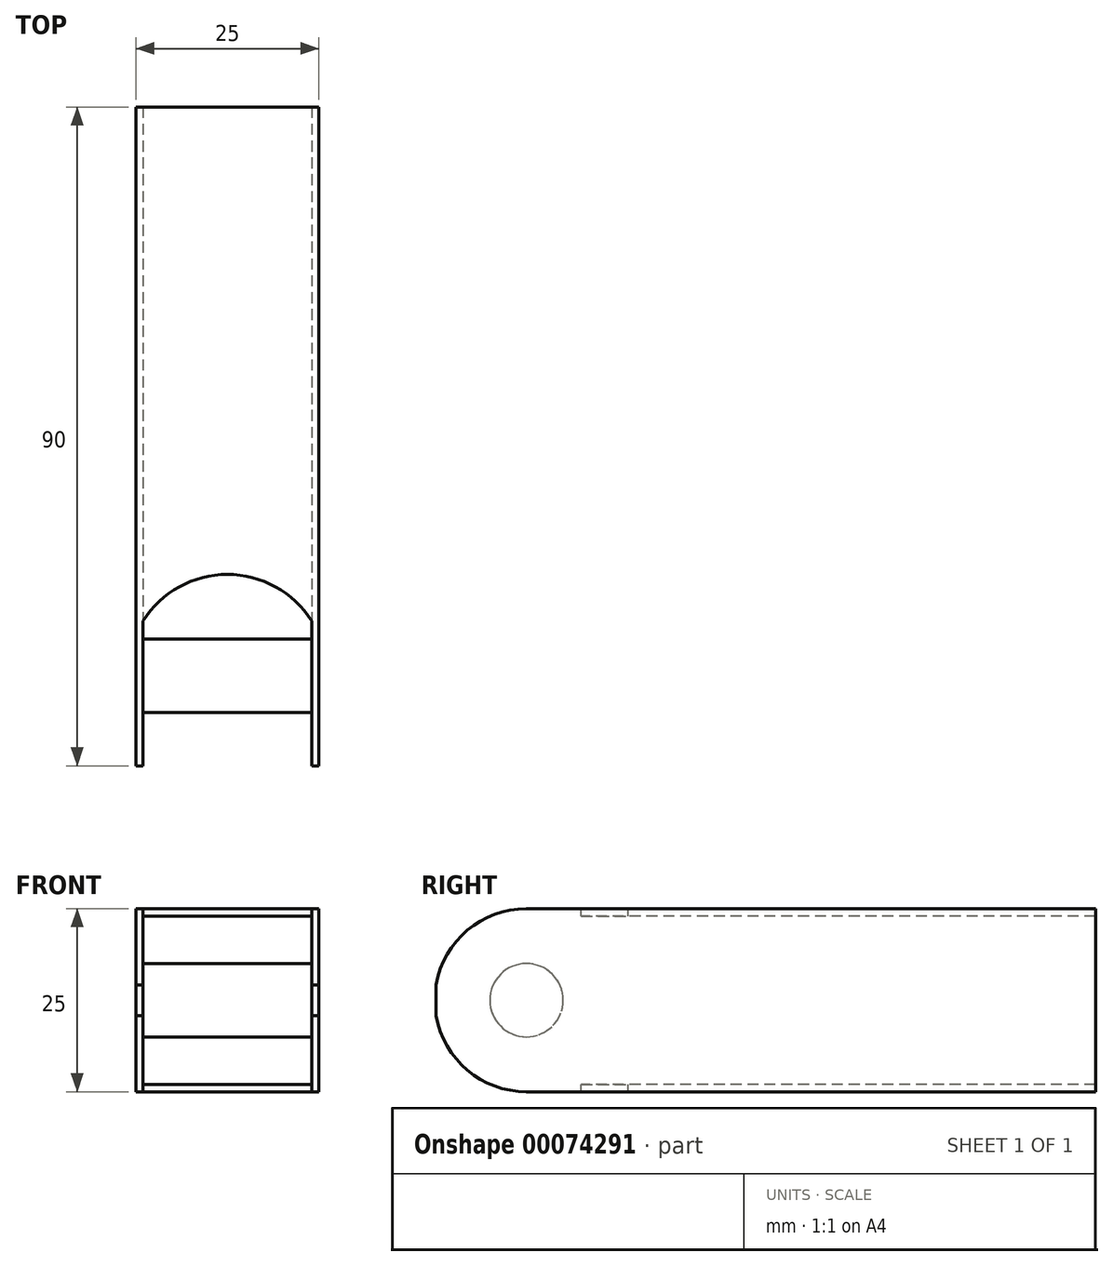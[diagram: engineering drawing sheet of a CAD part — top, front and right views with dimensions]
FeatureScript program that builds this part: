
annotation { "Feature Type Name" : "Feature", "Feature Type Description" : "" }
export const myFeature = defineFeature(function(context is Context, id is Id, definition is map)
    precondition{}
    {
        {
            var Q0;
            Q0=qCreatedBy(makeId("Front.planeOp"),FACE);
            var sketch = newSketch(context, id + "F0", { "sketchPlane" : qUnion([Q0])});
            skLineSegment(sketch, "E0.bottom", {"start": v(12.5, 12.5) * mm, "end": v(-12.5, 12.5) * mm});
            skLineSegment(sketch, "E0.top", {"start": v(12.5, -12.5) * mm, "end": v(-12.5, -12.5) * mm});
            skLineSegment(sketch, "E0.left", {"start": v(12.5, 12.5) * mm, "end": v(12.5, -12.5) * mm});
            skLineSegment(sketch, "E0.right", {"start": v(-12.5, 12.5) * mm, "end": v(-12.5, -12.5) * mm});
            skPoint(sketch, "E0.middle", {"position": v(0, 0) * mm});
            skSolve(sketch);
        }
        {
            var Q0;
            Q0 = qSketchRegion(id + "F0", true);
            extrude(context, id + "F1", {"entities" : qUnion([Q0]), "depth" : 75 * mm});
        }
        {
            var Q0;
            Q0=makeQuery(id+"F1.opExtrude","CAP_FACE",FACE,{"disambiguationData":[OSD([sQuery(id+"F0.wireOp",EDGE,"E0.bottom"),sQuery(id+"F0.wireOp",EDGE,"E0.top"),sQuery(id+"F0.wireOp",EDGE,"E0.left"),sQuery(id+"F0.wireOp",EDGE,"E0.right")])],"isStart":false});
            var sketch = newSketch(context, id + "F2", { "sketchPlane" : qUnion([Q0])});
            skLineSegment(sketch, "E1.0", {"start": v(-11.5, -11.5) * mm, "end": v(11.5, -11.5) * mm});
            skLineSegment(sketch, "E1.1", {"start": v(-11.5, 11.5) * mm, "end": v(-11.5, -11.5) * mm});
            skLineSegment(sketch, "E1.2", {"start": v(11.5, 11.5) * mm, "end": v(-11.5, 11.5) * mm});
            skLineSegment(sketch, "E1.3", {"start": v(11.5, -11.5) * mm, "end": v(11.5, 11.5) * mm});
            skSolve(sketch);
        }
        {
            var Q0;
            Q0 = qSketchRegion(id + "F2", true);
            extrude(context, id + "F3", {"entities" : qUnion([Q0]), "operationType" : NewBodyOperationType.REMOVE, "endBound" : BoundingType.THROUGH_ALL, "oppositeDirection" : true, "depth" : 25 * mm});
        }
        {
            var Q0;
            Q0=makeQuery(id+"F1.opExtrude","SWEPT_FACE",FACE,{"disambiguationData":[OSD([sQuery(id+"F0.wireOp",EDGE,"E0.left")])]});
            var sketch = newSketch(context, id + "F4", { "sketchPlane" : qUnion([Q0])});
            skLineSegment(sketch, "E2", {"start": v(-75, 0) * mm, "end": v(0, 0) * mm, "construction": true});
            skArc(sketch, "E3", {"start": v(-62.68, 12.5) * mm, "mid": v(-75.18, 0) * mm, "end": v(-62.68, -12.5) * mm});
            skLineSegment(sketch, "E4", {"start": v(-62.68, -12.5) * mm, "end": v(-60.3, -22.78) * mm});
            skLineSegment(sketch, "E5", {"start": v(-60.3, -22.78) * mm, "end": v(-83.69, -18.65) * mm});
            skLineSegment(sketch, "E6", {"start": v(-83.69, -18.65) * mm, "end": v(-82.12, 25.4) * mm});
            skLineSegment(sketch, "E7", {"start": v(-82.12, 25.4) * mm, "end": v(-62.68, 12.5) * mm});
            skSolve(sketch);
        }
        {
            var Q0;
            Q0 = qSketchRegion(id + "F4", true);
            extrude(context, id + "F5", {"entities" : qUnion([Q0]), "operationType" : NewBodyOperationType.REMOVE, "oppositeDirection" : true, "depth" : 25 * mm});
        }
        {
            var Q0;
            Q0=makeQuery(id+"F1.opExtrude","SWEPT_FACE",FACE,{"disambiguationData":[OSD([sQuery(id+"F0.wireOp",EDGE,"E0.bottom")])]});
            var sketch = newSketch(context, id + "F6", { "sketchPlane" : qUnion([Q0])});
            skLineSegment(sketch, "E8.0", {"start": v(-11.5, -75) * mm, "end": v(-11.5, -67.58) * mm});
            skLineSegment(sketch, "E9.0", {"start": v(11.5, -67.58) * mm, "end": v(11.5, -75) * mm});
            skLineSegment(sketch, "E10", {"start": v(-11.5, -67.58) * mm, "end": v(-11.5, -55.2) * mm});
            skLineSegment(sketch, "E11", {"start": v(-11.5, -55.2) * mm, "end": v(11.5, -55.2) * mm});
            skLineSegment(sketch, "E12", {"start": v(11.5, -55.2) * mm, "end": v(11.5, -67.58) * mm});
            skLineSegment(sketch, "E13", {"start": v(-11.5, -75) * mm, "end": v(11.5, -75) * mm});
            skSolve(sketch);
        }
        {
            var Q0;
            Q0 = qSketchRegion(id + "F6", true);
            extrude(context, id + "F7", {"entities" : qUnion([Q0]), "operationType" : NewBodyOperationType.REMOVE, "oppositeDirection" : true, "depth" : 25 * mm});
        }
        {
            var Q0;
            {var subQ0=sQuery(id+"F0.wireOp",EDGE,"E0.left");var subQ1=makeQuery(id+"F1.opExtrude","CAP_EDGE",EDGE,{"disambiguationData":[OSD([subQ0])],"isStart":true});Q0=makeQuery(id+"F4.imprint","IMPRINT",FACE,{"disambiguationData":[TD([[makeQuery(id+"F4.imprint","IMPRINT",EDGE,{"derivedFrom":subQ1}),-1.0]])]});}
            var sketch = newSketch(context, id + "F8", { "sketchPlane" : qUnion([Q0])});
            skCircle(sketch, "E14", {"center": v(-62.68, 0) * mm, "radius": 5 * mm});
            skSolve(sketch);
        }
        {
            var Q0;
            Q0=makeQuery(id+"F8.imprint","IMPRINT",FACE,{"disambiguationData":[TD([[makeQuery(id+"F8.imprint","IMPRINT",EDGE,{"derivedFrom":sQuery(id+"F8.wireOp",EDGE,"E14")}),1.0]])]});
            extrude(context, id + "F9", {"entities" : qUnion([Q0]), "operationType" : NewBodyOperationType.ADD, "oppositeDirection" : true, "depth" : 25 * mm});
        }
        {
            var Q0;
            Q0=makeQuery(id+"F1.opExtrude","SWEPT_FACE",FACE,{"disambiguationData":[OSD([sQuery(id+"F0.wireOp",EDGE,"E0.top")])]});
            var sketch = newSketch(context, id + "F10", { "sketchPlane" : qUnion([Q0])});
            skArc(sketch, "E15", {"start": v(-11.5, 55.2) * mm, "mid": v(0, 48.85) * mm, "end": v(11.5, 55.2) * mm});
            skLineSegment(sketch, "E16", {"start": v(11.5, 55.2) * mm, "end": v(-11.5, 55.2) * mm});
            skSolve(sketch);
        }
        {
            var Q0;
            Q0 = qSketchRegion(id + "F10", true);
            extrude(context, id + "F11", {"entities" : qUnion([Q0]), "operationType" : NewBodyOperationType.REMOVE, "oppositeDirection" : true, "depth" : 25 * mm});
        }
        {
            var Q0;
            Q0=makeQuery(id+"F0.imprint","IMPRINT",FACE,{"disambiguationData":[TD([[makeQuery(id+"F0.imprint","IMPRINT",EDGE,{"derivedFrom":sQuery(id+"F0.wireOp",EDGE,"E0.bottom")}),1.0]])]});
            var sketch = newSketch(context, id + "F12", { "sketchPlane" : qUnion([Q0])});
            skLineSegment(sketch, "E17.0", {"start": v(12.5, 12.5) * mm, "end": v(12.5, -12.5) * mm});
            skLineSegment(sketch, "E18.0", {"start": v(12.5, -12.5) * mm, "end": v(-12.5, -12.5) * mm});
            skLineSegment(sketch, "E19.0", {"start": v(12.5, 12.5) * mm, "end": v(-12.5, 12.5) * mm});
            skLineSegment(sketch, "E20.0", {"start": v(11.5, 11.5) * mm, "end": v(-11.5, 11.5) * mm});
            skLineSegment(sketch, "E21.0", {"start": v(11.5, -11.5) * mm, "end": v(11.5, 11.5) * mm});
            skLineSegment(sketch, "E22.0", {"start": v(-11.5, -11.5) * mm, "end": v(11.5, -11.5) * mm});
            skLineSegment(sketch, "E23.0", {"start": v(-11.5, 11.5) * mm, "end": v(-11.5, -11.5) * mm});
            skLineSegment(sketch, "E24.0", {"start": v(-12.5, 12.5) * mm, "end": v(-12.5, -12.5) * mm});
            skSolve(sketch);
        }
        {
            var Q0;
            Q0 = qSketchRegion(id + "F12", true);
            extrude(context, id + "F13", {"entities" : qUnion([Q0]), "operationType" : NewBodyOperationType.ADD, "oppositeDirection" : true, "depth" : 15 * mm});
        }
    });
